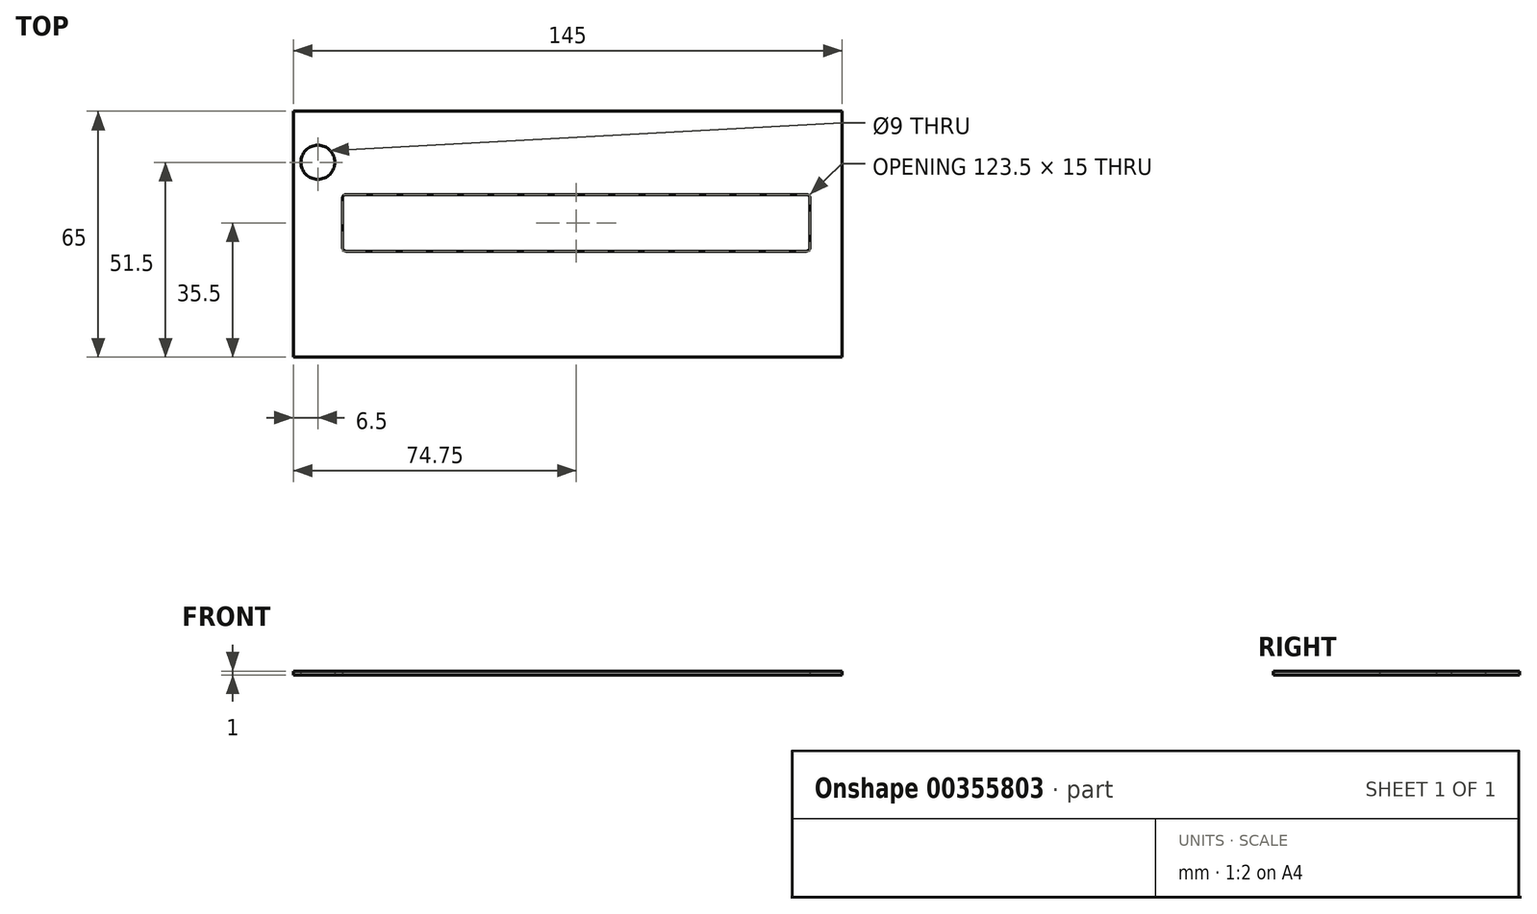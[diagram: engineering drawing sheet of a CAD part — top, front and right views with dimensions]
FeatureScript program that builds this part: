
annotation { "Feature Type Name" : "Feature", "Feature Type Description" : "" }
export const myFeature = defineFeature(function(context is Context, id is Id, definition is map)
    precondition{}
    {
        {
            var Q0;
            Q0=qCreatedBy(makeId("Top.planeOp"),FACE);
            var sketch = newSketch(context, id + "F0", { "sketchPlane" : qUnion([Q0])});
            skLineSegment(sketch, "E0.bottom", {"start": v(0, 0) * mm, "end": v(145, 0) * mm});
            skLineSegment(sketch, "E0.top", {"start": v(0, 65) * mm, "end": v(145, 65) * mm});
            skLineSegment(sketch, "E0.left", {"start": v(0, 0) * mm, "end": v(0, 65) * mm});
            skLineSegment(sketch, "E0.right", {"start": v(145, 0) * mm, "end": v(145, 65) * mm});
            skLineSegment(sketch, "E1.bottom", {"start": v(14, 43) * mm, "end": v(135.5, 43) * mm});
            skLineSegment(sketch, "E1.top", {"start": v(14, 28) * mm, "end": v(135.5, 28) * mm});
            skLineSegment(sketch, "E1.left", {"start": v(13, 42) * mm, "end": v(13, 29) * mm});
            skLineSegment(sketch, "E1.right", {"start": v(136.5, 42) * mm, "end": v(136.5, 29) * mm});
            skPoint(sketch, "E2.visualSharp", {"position": v(13, 43) * mm});
            skArc(sketch, "E2.filletArc", {"start": v(14, 43) * mm, "mid": v(13.3, 42.7) * mm, "end": v(13, 42) * mm});
            skPoint(sketch, "E3.visualSharp", {"position": v(136.5, 43) * mm});
            skArc(sketch, "E3.filletArc", {"start": v(136.5, 42) * mm, "mid": v(136.2, 42.7) * mm, "end": v(135.5, 43) * mm});
            skPoint(sketch, "E4.visualSharp", {"position": v(136.5, 28) * mm});
            skArc(sketch, "E4.filletArc", {"start": v(135.5, 28) * mm, "mid": v(136.2, 28.3) * mm, "end": v(136.5, 29) * mm});
            skPoint(sketch, "E5.visualSharp", {"position": v(13, 28) * mm});
            skArc(sketch, "E5.filletArc", {"start": v(13, 29) * mm, "mid": v(13.3, 28.3) * mm, "end": v(14, 28) * mm});
            skCircle(sketch, "E6", {"center": v(6.5, 51.5) * mm, "radius": 4.5 * mm});
            skSolve(sketch);
        }
        {
            var Q0;
            Q0=makeQuery(id+"F0.imprint","IMPRINT",FACE,{"disambiguationData":[TD([[makeQuery(id+"F0.imprint","IMPRINT",EDGE,{"derivedFrom":sQuery(id+"F0.wireOp",EDGE,"E0.bottom")}),1.0]])]});
            extrude(context, id + "F1", {"entities" : qUnion([Q0]), "depth" : 1 * mm});
        }
    });
